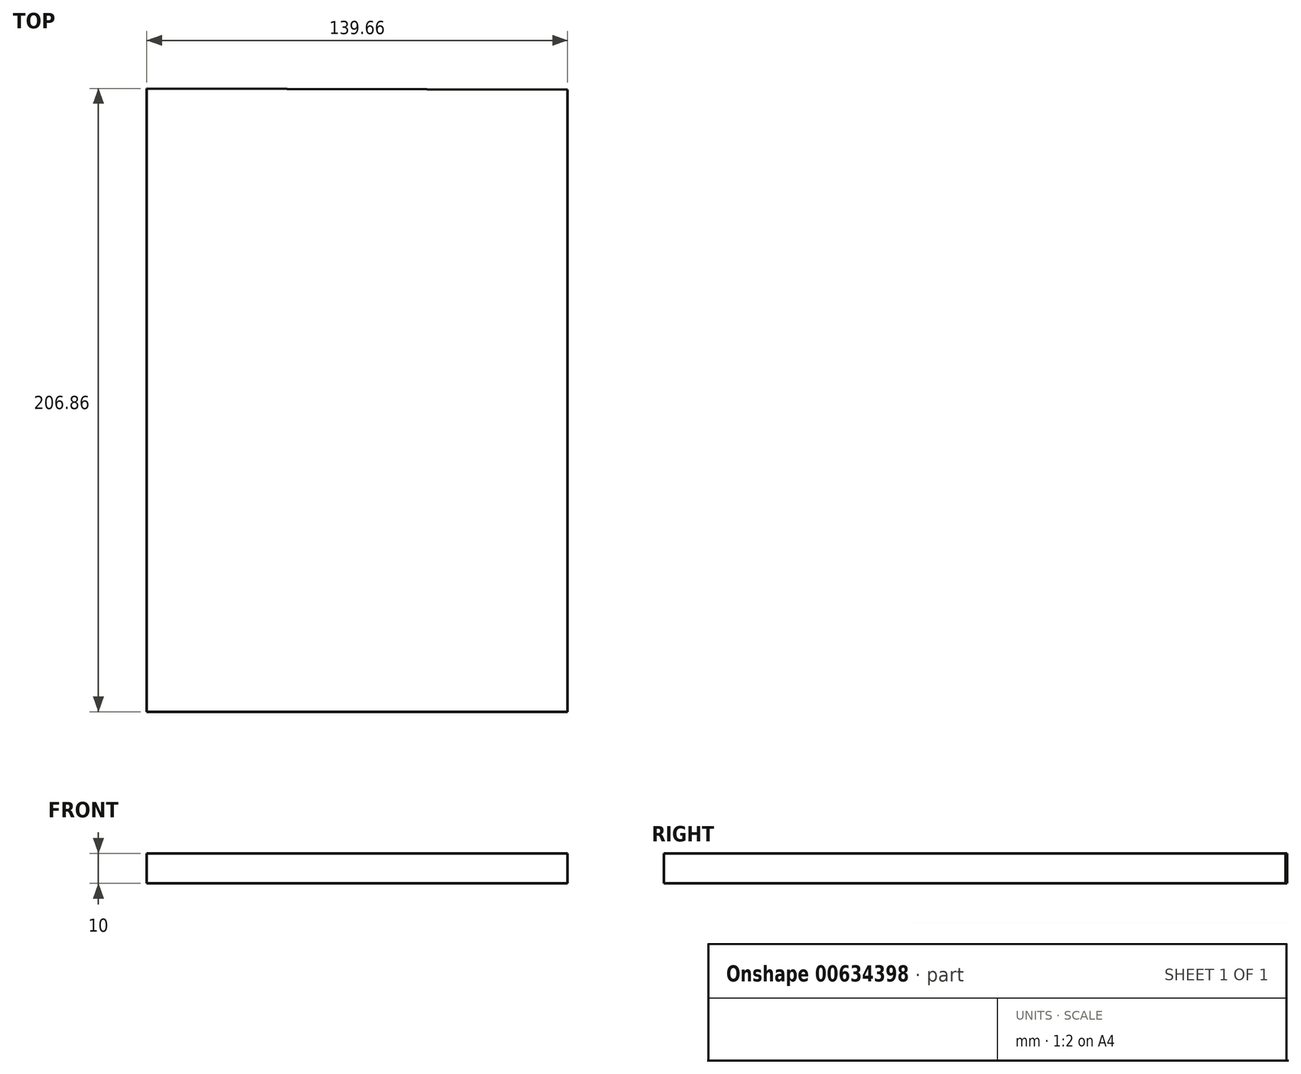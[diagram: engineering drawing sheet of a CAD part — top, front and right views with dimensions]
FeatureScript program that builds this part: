
annotation { "Feature Type Name" : "Feature", "Feature Type Description" : "" }
export const myFeature = defineFeature(function(context is Context, id is Id, definition is map)
    precondition{}
    {
        {
            var Q0;
            Q0=qCreatedBy(makeId("Top.planeOp"),FACE);
            var sketch = newSketch(context, id + "F0", { "sketchPlane" : qUnion([Q0])});
            skLineSegment(sketch, "E0", {"start": v(-64.4, 61.02) * mm, "end": v(-64.4, -145.84) * mm});
            skLineSegment(sketch, "E1", {"start": v(-64.4, -145.84) * mm, "end": v(75.25, -145.84) * mm});
            skLineSegment(sketch, "E2", {"start": v(75.25, -145.84) * mm, "end": v(75.25, 60.55) * mm});
            skLineSegment(sketch, "E3", {"start": v(75.25, 60.55) * mm, "end": v(-64.4, 61.02) * mm});
            skSolve(sketch);
        }
        {
            var Q0;
            Q0 = qSketchRegion(id + "F0", true);
            extrude(context, id + "F1", {"entities" : qUnion([Q0]), "depth" : 10 * mm, "offsetDistance" : 25.4 * mm});
        }
    });
